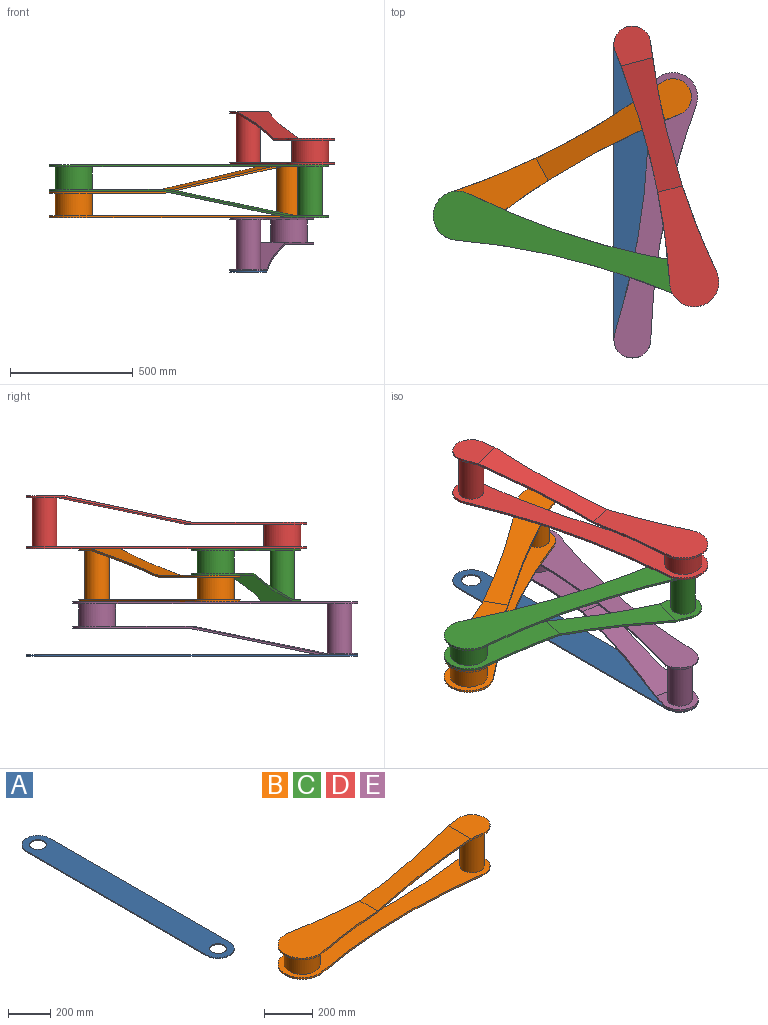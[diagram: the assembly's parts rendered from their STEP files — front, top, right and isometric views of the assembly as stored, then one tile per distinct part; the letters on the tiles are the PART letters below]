
ASSEMBLY  parts=5 mates=5
PART A: 8 faces, bbox 150x1350x5 mm
  f0: plane 1200x5mm, normal (1,0,0), area 6000mm2, adj f1,f4,f6,f7
  f1: cylinder r=75mm len=150mm, axis (0,0,-1), area 1178.1mm2, adj f0,f2,f6,f7
  f2: plane 1200x5mm, normal (-1,0,0), area 6000mm2, adj f1,f4,f6,f7
  f3: cylinder r=40mm len=80mm, axis (0,0,-1), area 1256.6mm2, adj f6,f7
  f4: cylinder r=75mm len=150mm, axis (0,0,-1), area 1178.1mm2, adj f0,f2,f6,f7
  f5: cylinder r=40mm len=80mm, axis (0,0,-1), area 1256.6mm2, adj f6,f7
  f6: plane 1350x150mm, normal (0,0,1), area 187618.4mm2, adj f0,f1,f2,f3,f4,f5
  f7: plane 1350x150mm, normal (0,0,-1), area 187618.4mm2, adj f0,f1,f2,f3,f4,f5
PART B: 18 faces, bbox 1175x200x216 mm
  f0: cylinder r=75mm len=150mm, axis (0,0,-1), area 2050.5mm2, adj f1,f3,f4,f5
  f1: cylinder r=3000mm len=971.07mm, axis (0,0,-1), area 7805.3mm2, adj f0,f2,f4,f5
  f2: cylinder r=100mm len=200mm, axis (0,0,-1), area 2812.9mm2, adj f1,f3,f4,f5
  f3: cylinder r=3000mm len=971.07mm, axis (0,0,-1), area 7805.3mm2, adj f0,f2,f4,f5
  f4: plane 1175x200mm, normal (0,0,1), area 120485.2mm2, adj f0,f1,f2,f3,f6,f7
  f5: plane 1175x200mm, normal (0,0,-1), area 146010.7mm2, adj f0,f1,f2,f3
  f6: cylinder r=75mm len=150mm, axis (0,0,-1), area 43354mm2, adj f4,f8
  f7: cylinder r=50mm len=200mm, axis (0,0,-1), area 62831.9mm2, adj f4,f10
  f8: plane 492.51x200mm, normal (0,0,-1), area 54746.9mm2, adj f6,f9,f11,f12,f13
  f9: plane 535.39x132.73mm, normal (0.2,0,-0.98), area 55635.4mm2, adj f8,f10,f12,f13
  f10: plane 150x147.11mm, normal (0,0,-1), area 11201.5mm2, adj f7,f9,f12,f13,f14
  f11: cylinder r=100mm len=200mm, axis (0,0,1), area 2812.9mm2, adj f8,f12,f13,f15
  f12: cylinder r=3000mm len=971.07mm, axis (0,0,1), area 7891.7mm2, adj f8,f9,f10,f11,f14,f15,f16,f17
  f13: cylinder r=3000mm len=971.07mm, axis (0,0,1), area 7891.7mm2, adj f8,f9,f10,f11,f14,f15,f16,f17
  f14: cylinder r=75mm len=150mm, axis (0,0,1), area 2050.5mm2, adj f10,f12,f13,f17
  f15: plane 491.71x200mm, normal (0,0,1), area 72336.1mm2, adj f11,f12,f13,f16
  f16: plane 535.39x132.54mm, normal (-0.2,0,0.98), area 55611.2mm2, adj f12,f13,f15,f17
  f17: plane 150x147.9mm, normal (0,0,1), area 19161.4mm2, adj f12,f13,f14,f16
PART C: same geometry as B
PART D: same geometry as B
PART E: same geometry as B
PLACE A t=(-2165.02,1322.51,536.01)mm fixed
PLACE B rot(axis=(0,0,1),28.8deg) t=(-2181.04,1998.7,757.01)mm
PLACE C rot(axis=(-0.99,0.14,0),180deg) t=(-2094.61,1244.8,973.01)mm
PLACE D rot(axis=(0,0,1),104.6deg) t=(-2346.67,2212.51,973.01)mm
PLACE E rot(axis=(0.65,-0.76,0),180deg) t=(-2346.67,1012.51,757.01)mm
MATE revolute B.f11 <-> C.f11  axis (0,0,1) through (-3057.03,1516.36,865.01)mm
MATE cylindrical D.f7 <-> A.f1  axis (0,0,-1) through (-2346.67,2212.51,1081.01)mm
MATE revolute D.f2 <-> C.f0  axis (0,0,-1) through (-2094.61,1244.8,973.01)mm
MATE revolute B.f0 <-> E.f2  axis (0,0,-1) through (-2181.04,1998.7,757.01)mm
MATE revolute E.f14 <-> A.f3  axis (0,0,-1) through (-2346.67,1012.51,541.01)mm
